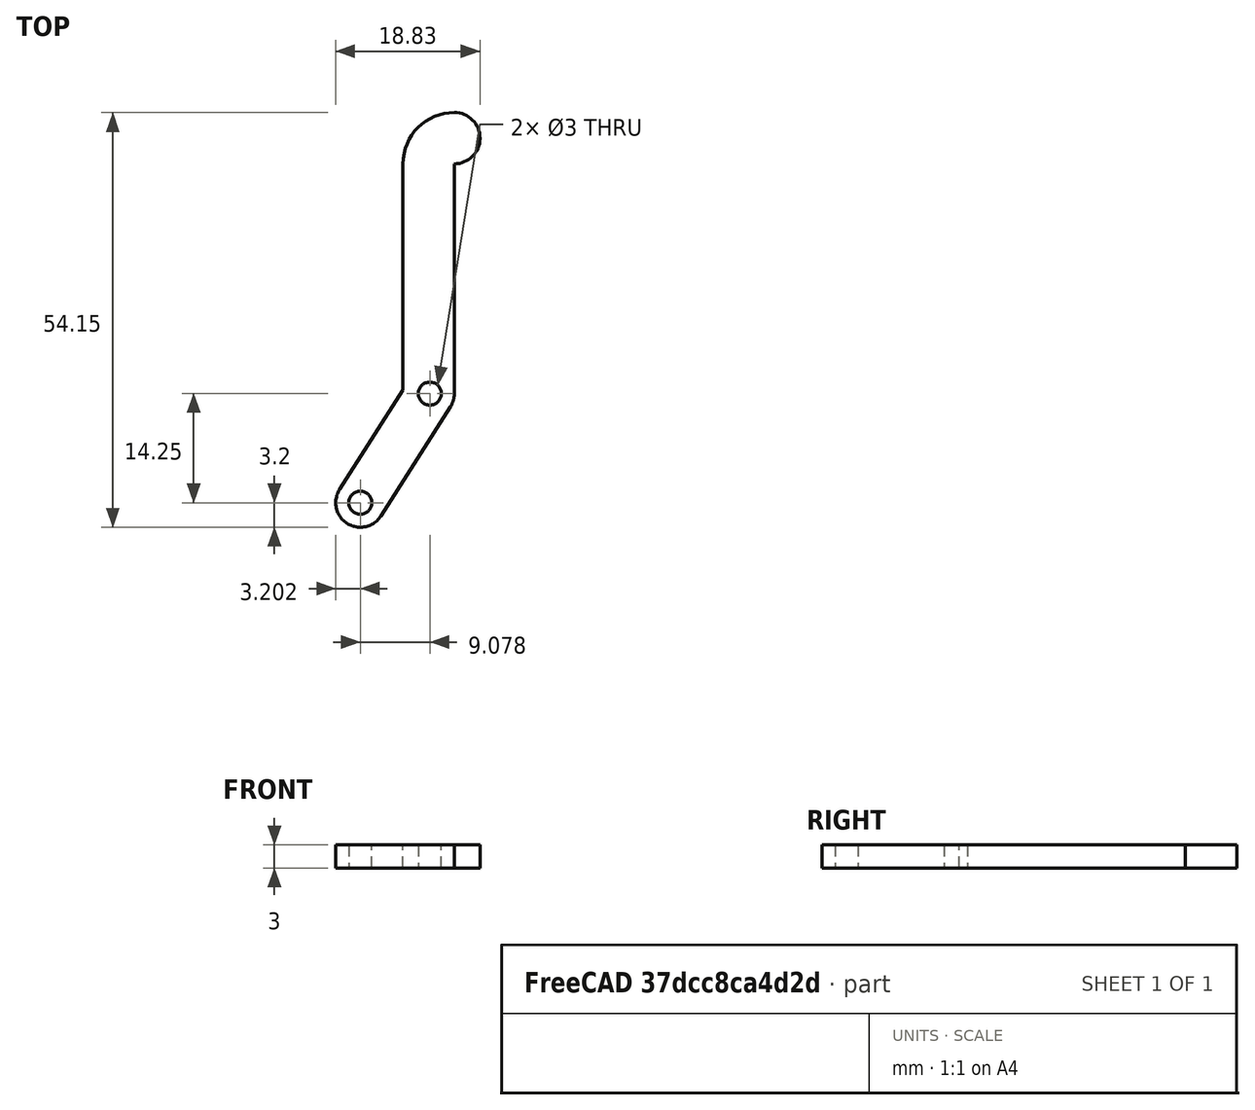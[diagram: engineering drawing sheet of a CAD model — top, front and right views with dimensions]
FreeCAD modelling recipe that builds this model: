
FCSTD DOCUMENT  (FreeCAD 0.18.1R)
Label: trigger
License: All rights reserved
LicenseURL: http://en.wikipedia.org/wiki/All_rights_reserved
objects: Sketcher::SketchObject×1, PartDesign::Pad×1, PartDesign::Body×1, TechDraw::DrawSVGTemplate×1, TechDraw::DrawViewPart×1, TechDraw::DrawPage×1, Spreadsheet::Sheet×1
note: 4 computed .brp shape members not serialized (recipe doc carries the construction recipe); baked Part::Feature solids carry a one-line shape summary decoded from their .brp

FEATURE [Sketcher::SketchObject] Sketch
  MapMode = 5
  Support = -> [XY_Plane]
  sketch-geometry (15):
    g0: LineSegment [constr] StartX=0 StartY=0 StartZ=0 EndX=-9.07825 EndY=-14.25 EndZ=0
    g1: LineSegment [constr] StartX=0 StartY=0 StartZ=0 EndX=0 EndY=-17.75 EndZ=0
    g2: ArcOfCircle CenterX=-9.07825 CenterY=-14.25 CenterZ=0 NormalX=0 NormalY=0 NormalZ=1 AngleXU=0 Radius=3.2 StartAngle=2.57436 EndAngle=5.71595
    g3: LineSegment StartX=-11.7771 StartY=-12.5306 StartZ=0 EndX=-3.5 EndY=0.461809 EndZ=0
    g4: LineSegment StartX=-3.5 StartY=0.461809 StartZ=0 EndX=-3.5 EndY=30 EndZ=0
    g5: LineSegment StartX=3.2 StartY=30 StartZ=0 EndX=3.2 EndY=0 EndZ=0
    g6: LineSegment StartX=-6.3794 StartY=-15.9694 StartZ=0 EndX=2.69885 EndY=-1.71936 EndZ=0
    g7: ArcOfCircle CenterX=0 CenterY=0 CenterZ=0 NormalX=0 NormalY=0 NormalZ=1 AngleXU=0 Radius=3.2 StartAngle=5.71595 EndAngle=6.28319
    g8: Circle CenterX=-9.07825 CenterY=-14.25 CenterZ=0 NormalX=0 NormalY=0 NormalZ=1 AngleXU=0 Radius=1.5
    g9: Circle CenterX=0 CenterY=0 CenterZ=0 NormalX=0 NormalY=0 NormalZ=1 AngleXU=0 Radius=1.5
    g10: ArcOfCircle CenterX=3.2 CenterY=30 CenterZ=0 NormalX=0 NormalY=0 NormalZ=1 AngleXU=0 Radius=6.7 StartAngle=1.5708 EndAngle=3.14159
    g11: ArcOfCircle CenterX=3.2 CenterY=33.35 CenterZ=0 NormalX=0 NormalY=0 NormalZ=1 AngleXU=0 Radius=3.35 StartAngle=4.71239 EndAngle=7.85398
    g12: LineSegment [constr] StartX=0 StartY=0 StartZ=0 EndX=18.6803 EndY=9.03367 EndZ=0
    g13: LineSegment [constr] StartX=18.6803 StartY=9.03367 StartZ=0 EndX=4.61195 EndY=38.1251 EndZ=0
    g14: LineSegment [constr] StartX=0.283095 StartY=36.0317 StartZ=0 EndX=4.61195 EndY=38.1251 EndZ=0
  constraints (40):
    c: Coincident(g0,g-1)
    c: Coincident(g1,g-1)
    c: PointOnObject(g1,g-2)
    c: DistanceY(g1,g1) = 17.75
    c: DistanceY(g1,g0) = 3.5
    c: Coincident(g2,g0)
    c: Coincident(g4,g3)
    c: Parallel(g3,g0)
    c: Vertical(g4)
    c: Vertical(g5)
    c: Parallel(g6,g0)
    c: Coincident(g7,g-1)
    c: Tangent(g7,g5) = 1.5708
    c: Coincident(g8,g2)
    c: Coincident(g9,g7)
    c: Diameter(g9) = 3
    c: Diameter(g8) = 3
    c: Coincident(g10,g5)
    c: Vertical(g10,g5)
    c: Coincident(g5,g11)
    c: DistanceX(g3,g7) = 3.5
    c: Tangent(g11,g10) = -1.5708
    c: Tangent(g10,g4) = 1.5708
    c: Tangent(g2,g3) = 1.5708
    c: Tangent(g6,g2) = -1.5708
    c: DistanceY(g4) = 30
    c: Distance(g2,g2) = 3.2
    c: Tangent(g6,g7) = -1.5708
    c: Coincident(g12,g7)
    c: Coincident(g13,g12)
    c: Perpendicular(g12,g13)
    c: Distance(g12) = 20.75
    c: Tangent(g11,g13)
    c: Angle(g12,g-2) = 1.12036
    c: Angle(g0,g1) = 0.567232
    c: PointOnObject(g14,g10)
    c: Coincident(g14,g13)
    c: Tangent(g14,g10)
    c: Perpendicular(g13,g14)
    c: Distance(g13) = 32.3146  'offset'
FEATURE [PartDesign::Pad] Pad
  Length = 3
  Length2 = 100
  Profile = -> Sketch
  Refine = true
  Type = 0
FEATURE [PartDesign::Body] Body  label="trigger"
  Group = -> [Sketch,Pad]
  Origin = -> Origin
  Tip = -> Pad
FEATURE [TechDraw::DrawSVGTemplate] Template
  Height = 297
  Orientation = 0
  Width = 210
FEATURE [TechDraw::DrawViewPart] View
  CoarseView = false
  Direction = (0,0,1)
  Focus = 100
  HardHidden = false
  IsoCount = 0
  IsoHidden = false
  IsoVisible = false
  LockPosition = false
  Perspective = false
  Rotation = 0
  ScaleType = 0
  SeamHidden = false
  SeamVisible = false
  SmoothHidden = false
  SmoothVisible = false
  Source = -> [Pad]
  X = 63.9512
  Y = 218.524
FEATURE [TechDraw::DrawPage] Page  label="Trigger Drawing"
  KeepUpdated = true
  ProjectionType = 0
  Template = -> Template
  Views = -> [View]
FEATURE [Spreadsheet::Sheet] Spreadsheet  label="values"
  cells = A1=Offset; B1(offset)==Sketch.Constraints.offset
